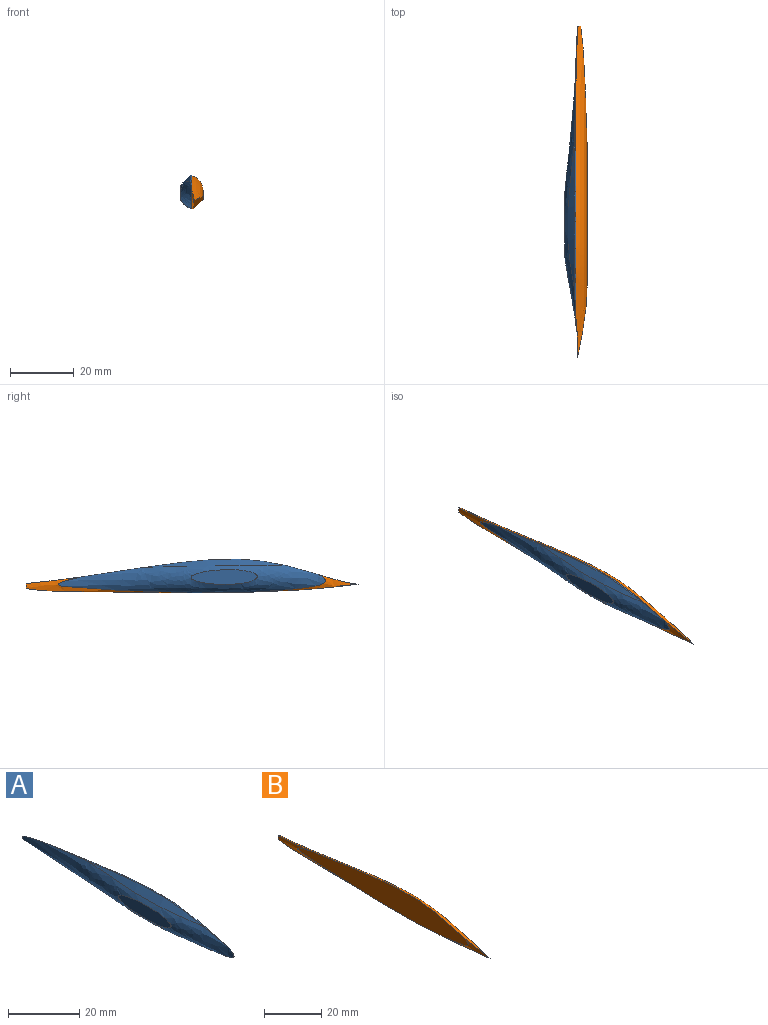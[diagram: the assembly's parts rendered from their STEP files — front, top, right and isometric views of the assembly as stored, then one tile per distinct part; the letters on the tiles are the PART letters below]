
ASSEMBLY  parts=2 mates=1
PART A: 5 faces, bbox 22.7x97.3x19.9 mm
  f0: bspline ~88.39x11.88mm, area 646.8mm2, adj f1,f2,f3,f4
  f1: bspline ~62.35x7.53mm, area 0mm2, adj f0,f3
  f2: plane 85.98x12.48mm, normal (1,0,0), area 604.3mm2, adj f0,f3
  f3: bspline ~81.56x10.97mm, area 31.4mm2, adj f0,f1,f2
  f4: plane 29.78x13.63mm, normal (1,0,0), area 76.3mm2, adj f0
PART B: 6 faces, bbox 14.8x116.6x13.6 mm
  f0: plane 45.25x4.14mm, normal (1,0,0), area 77mm2, adj f1,f4
  f1: bspline ~115.55x6.68mm, area 369.1mm2, adj f0,f2,f3,f4
  f2: plane 1.66x1.13mm, normal (0,1,0.06), area 0.9mm2, adj f1,f3,f4
  f3: bspline ~106.72x12.2mm, area 107.7mm2, adj f1,f2,f4,f5
  f4: bspline ~106.22x12.54mm, area 502.2mm2, adj f0,f1,f2,f3,f5
  f5: plane 84.04x10.54mm, normal (-1,0,0), area 604.3mm2, adj f3,f4
PLACE A t=(0.18,49.51,-29.7)mm
PLACE B t=(0.18,49.51,-29.7)mm
MATE planar A.f2 <-> B.f5  axis (1,0,0) through (3.68,-18.91,-29.69)mm
